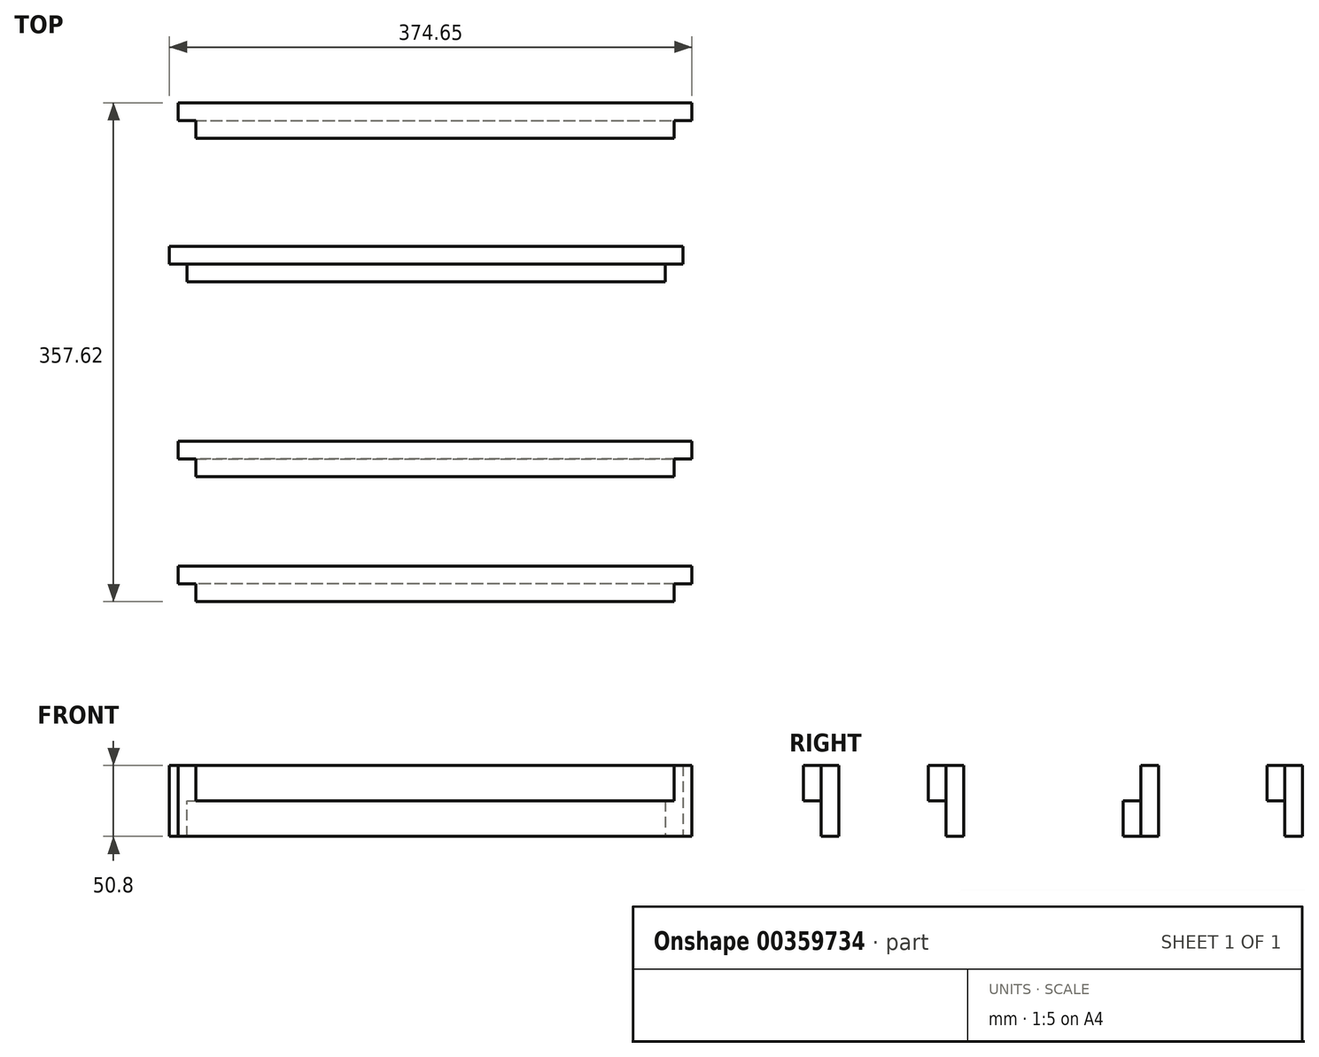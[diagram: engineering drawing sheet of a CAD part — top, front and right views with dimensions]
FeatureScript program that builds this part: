
annotation { "Feature Type Name" : "Feature", "Feature Type Description" : "" }
export const myFeature = defineFeature(function(context is Context, id is Id, definition is map)
    precondition{}
    {
        {
            var Q0;
            Q0=qCreatedBy(makeId("Top.planeOp"),FACE);
            var sketch = newSketch(context, id + "F0", { "sketchPlane" : qUnion([Q0])});
            skLineSegment(sketch, "E0.bottom", {"start": v(-184.15, 57.47) * mm, "end": v(184.15, 57.47) * mm});
            skLineSegment(sketch, "E0.top", {"start": v(-184.15, 32.07) * mm, "end": v(184.15, 32.07) * mm});
            skLineSegment(sketch, "E0.left", {"start": v(-184.15, 57.47) * mm, "end": v(-184.15, 32.07) * mm});
            skLineSegment(sketch, "E0.right", {"start": v(184.15, 57.47) * mm, "end": v(184.15, 32.07) * mm});
            skLineSegment(sketch, "E1.MirrorCS", {"start": v(-184.15, -32.07) * mm, "end": v(184.15, -32.07) * mm});
            skLineSegment(sketch, "E2.MirrorCS", {"start": v(-184.15, -57.47) * mm, "end": v(-184.15, -32.07) * mm});
            skLineSegment(sketch, "E3.MirrorCS", {"start": v(-184.15, -57.47) * mm, "end": v(184.15, -57.47) * mm});
            skLineSegment(sketch, "E4.MirrorCS", {"start": v(184.15, -57.47) * mm, "end": v(184.15, -32.07) * mm});
            skLineSegment(sketch, "E5.MirrorCS", {"start": v(-190.5, 274.75) * mm, "end": v(190.5, 274.75) * mm});
            skLineSegment(sketch, "E6.MirrorCS", {"start": v(-190.5, 300.15) * mm, "end": v(190.5, 300.15) * mm});
            skLineSegment(sketch, "E7.MirrorCS", {"start": v(-184.15, 274.75) * mm, "end": v(-184.15, 301.06) * mm});
            skLineSegment(sketch, "E8.MirrorCS", {"start": v(184.15, 274.75) * mm, "end": v(184.15, 301.06) * mm});
            skLineSegment(sketch, "E9.MirrorCS", {"start": v(-190.5, 171.65) * mm, "end": v(177.8, 171.65) * mm});
            skLineSegment(sketch, "E10.MirrorCS", {"start": v(-196.85, 197.05) * mm, "end": v(184.15, 197.05) * mm});
            skLineSegment(sketch, "E11.MirrorCS", {"start": v(-190.5, 170.74) * mm, "end": v(-190.5, 197.05) * mm});
            skLineSegment(sketch, "E12.MirrorCS", {"start": v(177.8, 170.74) * mm, "end": v(177.8, 197.05) * mm});
            skLineSegment(sketch, "E13", {"start": v(-6.35, 171.65) * mm, "end": v(-6.35, 197.05) * mm});
            skLineSegment(sketch, "E14", {"start": v(0, 274.75) * mm, "end": v(0, 300.15) * mm});
            skLineSegment(sketch, "E15", {"start": v(0, -57.47) * mm, "end": v(0, -32.07) * mm});
            skSolve(sketch);
        }
        {
            var Q0;
            Q0 = qSketchRegion(id + "F0", true);
            extrude(context, id + "F1", {"entities" : qUnion([Q0]), "depth" : 50.8 * mm});
        }
        {
            var Q0;
            Q0=makeQuery(id+"F1.opExtrude","CAP_FACE",FACE,{"disambiguationData":[OSD([sQuery(id+"F0.wireOp",EDGE,"E5.MirrorCS"),sQuery(id+"F0.wireOp",EDGE,"E6.MirrorCS"),sQuery(id+"F0.wireOp",EDGE,"E7.MirrorCS"),sQuery(id+"F0.wireOp",EDGE,"E8.MirrorCS")])],"isStart":false});
            var sketch = newSketch(context, id + "F2", { "sketchPlane" : qUnion([Q0])});
            skLineSegment(sketch, "E16", {"start": v(-184.15, 287.45) * mm, "end": v(-171.45, 287.45) * mm});
            skLineSegment(sketch, "E17", {"start": v(-171.45, 287.45) * mm, "end": v(-171.45, 274.75) * mm});
            skLineSegment(sketch, "E18", {"start": v(-171.45, 274.75) * mm, "end": v(-184.15, 274.75) * mm});
            skLineSegment(sketch, "E19", {"start": v(-184.15, 274.75) * mm, "end": v(-184.15, 287.45) * mm});
            skLineSegment(sketch, "E20", {"start": v(0, 274.75) * mm, "end": v(0, 300.15) * mm});
            skLineSegment(sketch, "E21.MirrorCS", {"start": v(184.15, 287.45) * mm, "end": v(171.45, 287.45) * mm});
            skLineSegment(sketch, "E22.MirrorCS", {"start": v(171.45, 287.45) * mm, "end": v(171.45, 274.75) * mm});
            skLineSegment(sketch, "E23.MirrorCS", {"start": v(171.45, 274.75) * mm, "end": v(184.15, 274.75) * mm});
            skLineSegment(sketch, "E24.MirrorCS", {"start": v(184.15, 274.75) * mm, "end": v(184.15, 287.45) * mm});
            skSolve(sketch);
        }
        {
            var Q0;
            Q0=makeQuery(id+"F2.imprint","IMPRINT",FACE,{"disambiguationData":[TD([[makeQuery(id+"F2.imprint","IMPRINT",EDGE,{"derivedFrom":sQuery(id+"F2.wireOp",EDGE,"E16")}),-1.0]])]});
            extrude(context, id + "F3", {"entities" : qUnion([Q0]), "operationType" : NewBodyOperationType.REMOVE, "oppositeDirection" : true, "depth" : 61.2 * mm});
        }
        {
            var Q0;
            Q0=makeQuery(id+"F1.opExtrude","CAP_FACE",FACE,{"disambiguationData":[OSD([sQuery(id+"F0.wireOp",EDGE,"E9.MirrorCS"),sQuery(id+"F0.wireOp",EDGE,"E10.MirrorCS"),sQuery(id+"F0.wireOp",EDGE,"E11.MirrorCS"),sQuery(id+"F0.wireOp",EDGE,"E12.MirrorCS")])],"isStart":false});
            var sketch = newSketch(context, id + "F4", { "sketchPlane" : qUnion([Q0])});
            skPoint(sketch, "E25.oppositeSnap0", {"position": v(-190.5, 184.35) * mm});
            skLineSegment(sketch, "E25.bottom", {"start": v(-190.5, 171.65) * mm, "end": v(-177.8, 171.65) * mm});
            skLineSegment(sketch, "E25.top", {"start": v(-190.5, 184.35) * mm, "end": v(-177.8, 184.35) * mm});
            skLineSegment(sketch, "E25.left", {"start": v(-190.5, 171.65) * mm, "end": v(-190.5, 184.35) * mm});
            skLineSegment(sketch, "E25.right", {"start": v(-177.8, 171.65) * mm, "end": v(-177.8, 184.35) * mm});
            skSolve(sketch);
        }
        {
            var Q0;
            Q0 = qSketchRegion(id + "F4", true);
            extrude(context, id + "F5", {"entities" : qUnion([Q0]), "operationType" : NewBodyOperationType.REMOVE, "oppositeDirection" : true, "depth" : 76.2 * mm});
        }
        {
            var Q0;
            Q0=makeQuery(id+"F1.opExtrude","SWEPT_FACE",FACE,{"disambiguationData":[OSD([sQuery(id+"F0.wireOp",EDGE,"E0.left")])]});
            var sketch = newSketch(context, id + "F6", { "sketchPlane" : qUnion([Q0])});
            skLineSegment(sketch, "E26.bottom", {"start": v(-44.77, 0) * mm, "end": v(-32.07, 0) * mm});
            skLineSegment(sketch, "E26.top", {"start": v(-44.77, 50.8) * mm, "end": v(-32.07, 50.8) * mm});
            skLineSegment(sketch, "E26.left", {"start": v(-44.77, 0) * mm, "end": v(-44.77, 50.8) * mm});
            skLineSegment(sketch, "E26.right", {"start": v(-32.07, 0) * mm, "end": v(-32.07, 50.8) * mm});
            skSolve(sketch);
        }
        {
            var Q0;
            Q0 = qSketchRegion(id + "F6", true);
            extrude(context, id + "F7", {"entities" : qUnion([Q0]), "operationType" : NewBodyOperationType.REMOVE, "oppositeDirection" : true, "depth" : 12.7 * mm});
        }
        {
            var Q0;
            Q0=makeQuery(id+"F1.opExtrude","SWEPT_FACE",FACE,{"disambiguationData":[OSD([sQuery(id+"F0.wireOp",EDGE,"E2.MirrorCS")])]});
            var sketch = newSketch(context, id + "F8", { "sketchPlane" : qUnion([Q0])});
            skLineSegment(sketch, "E27.bottom", {"start": v(44.77, 0) * mm, "end": v(57.47, 0) * mm});
            skLineSegment(sketch, "E27.top", {"start": v(44.77, 50.8) * mm, "end": v(57.47, 50.8) * mm});
            skLineSegment(sketch, "E27.left", {"start": v(44.77, 0) * mm, "end": v(44.77, 50.8) * mm});
            skLineSegment(sketch, "E27.right", {"start": v(57.47, 0) * mm, "end": v(57.47, 50.8) * mm});
            skSolve(sketch);
        }
        {
            var Q0;
            Q0 = qSketchRegion(id + "F8", true);
            extrude(context, id + "F9", {"entities" : qUnion([Q0]), "operationType" : NewBodyOperationType.REMOVE, "oppositeDirection" : true, "depth" : 12.7 * mm});
        }
        {
            var Q0;
            Q0 = qSketchRegion(id + "F2", true);
            extrude(context, id + "F10", {"entities" : qUnion([Q0]), "operationType" : NewBodyOperationType.REMOVE, "oppositeDirection" : true, "depth" : 50.8 * mm});
        }
        {
            var Q0;
            Q0=makeQuery(id+"F1.opExtrude","SWEPT_FACE",FACE,{"disambiguationData":[OSD([sQuery(id+"F0.wireOp",EDGE,"E12.MirrorCS")])]});
            var sketch = newSketch(context, id + "F11", { "sketchPlane" : qUnion([Q0])});
            skLineSegment(sketch, "E28.bottom", {"start": v(184.35, 50.8) * mm, "end": v(171.65, 50.8) * mm});
            skLineSegment(sketch, "E28.top", {"start": v(184.35, 0) * mm, "end": v(171.65, 0) * mm});
            skLineSegment(sketch, "E28.left", {"start": v(184.35, 50.8) * mm, "end": v(184.35, 0) * mm});
            skLineSegment(sketch, "E28.right", {"start": v(171.65, 50.8) * mm, "end": v(171.65, 0) * mm});
            skSolve(sketch);
        }
        {
            var Q0;
            Q0=makeQuery(id+"F11.imprint","IMPRINT",FACE,{"disambiguationData":[TD([[makeQuery(id+"F11.imprint","IMPRINT",EDGE,{"derivedFrom":sQuery(id+"F11.wireOp",EDGE,"E28.bottom")}),-1.0]])]});
            extrude(context, id + "F12", {"entities" : qUnion([Q0]), "operationType" : NewBodyOperationType.REMOVE, "oppositeDirection" : true, "depth" : 12.7 * mm});
        }
        {
            var Q0;
            Q0=makeQuery(id+"F1.opExtrude","SWEPT_FACE",FACE,{"disambiguationData":[OSD([sQuery(id+"F0.wireOp",EDGE,"E0.right")])]});
            var sketch = newSketch(context, id + "F13", { "sketchPlane" : qUnion([Q0])});
            skLineSegment(sketch, "E29.bottom", {"start": v(44.77, 50.8) * mm, "end": v(32.07, 50.8) * mm});
            skLineSegment(sketch, "E29.top", {"start": v(44.77, 0) * mm, "end": v(32.07, 0) * mm});
            skLineSegment(sketch, "E29.left", {"start": v(44.77, 50.8) * mm, "end": v(44.77, 0) * mm});
            skLineSegment(sketch, "E29.right", {"start": v(32.07, 50.8) * mm, "end": v(32.07, 0) * mm});
            skSolve(sketch);
        }
        {
            var Q0;
            Q0 = qSketchRegion(id + "F13", true);
            extrude(context, id + "F14", {"entities" : qUnion([Q0]), "operationType" : NewBodyOperationType.REMOVE, "oppositeDirection" : true, "depth" : 12.7 * mm});
        }
        {
            var Q0;
            Q0=makeQuery(id+"F1.opExtrude","CAP_FACE",FACE,{"disambiguationData":[OSD([sQuery(id+"F0.wireOp",EDGE,"E1.MirrorCS"),sQuery(id+"F0.wireOp",EDGE,"E2.MirrorCS"),sQuery(id+"F0.wireOp",EDGE,"E3.MirrorCS"),sQuery(id+"F0.wireOp",EDGE,"E4.MirrorCS")])],"isStart":true});
            var sketch = newSketch(context, id + "F15", { "sketchPlane" : qUnion([Q0])});
            skLineSegment(sketch, "E30", {"start": v(184.15, 44.77) * mm, "end": v(171.45, 44.77) * mm});
            skPoint(sketch, "E30.endSnap0", {"position": v(184.15, 44.77) * mm});
            skLineSegment(sketch, "E31", {"start": v(171.45, 44.77) * mm, "end": v(171.45, 32.07) * mm});
            skLineSegment(sketch, "E32", {"start": v(171.45, 32.07) * mm, "end": v(184.15, 32.07) * mm});
            skLineSegment(sketch, "E33", {"start": v(184.15, 32.07) * mm, "end": v(184.15, 44.77) * mm});
            skLineSegment(sketch, "E34", {"start": v(171.45, 44.77) * mm, "end": v(171.45, 57.47) * mm});
            skLineSegment(sketch, "E35", {"start": v(171.45, 57.47) * mm, "end": v(184.15, 57.47) * mm});
            skLineSegment(sketch, "E36", {"start": v(184.15, 57.47) * mm, "end": v(184.15, 44.77) * mm});
            skSolve(sketch);
        }
        {
            var Q0;
            Q0=makeQuery(id+"F15.imprint","IMPRINT",FACE,{"disambiguationData":[TD([[makeQuery(id+"F15.imprint","IMPRINT",EDGE,{"derivedFrom":sQuery(id+"F15.wireOp",EDGE,"E30")}),-1.0]])]});
            extrude(context, id + "F16", {"entities" : qUnion([Q0]), "operationType" : NewBodyOperationType.REMOVE, "oppositeDirection" : true, "depth" : 90.68 * mm});
        }
        {
            var Q0;
            Q0=makeQuery(id+"F9.boolean.opBoolean","COPY",FACE,{"derivedFrom":makeQuery(id+"F9.opExtrude","CAP_FACE",FACE,{"disambiguationData":[OSD([sQuery(id+"F8.wireOp",EDGE,"E27.bottom"),sQuery(id+"F8.wireOp",EDGE,"E27.top"),sQuery(id+"F8.wireOp",EDGE,"E27.left"),sQuery(id+"F8.wireOp",EDGE,"E27.right")])],"isStart":false})});
            var sketch = newSketch(context, id + "F17", { "sketchPlane" : qUnion([Q0])});
            skLineSegment(sketch, "E37", {"start": v(44.77, 50.8) * mm, "end": v(44.77, 0) * mm});
            skLineSegment(sketch, "E38", {"start": v(44.77, 0) * mm, "end": v(44.77, 25.4) * mm});
            skLineSegment(sketch, "E39", {"start": v(44.77, 25.4) * mm, "end": v(57.47, 25.4) * mm});
            skLineSegment(sketch, "E40", {"start": v(57.47, 25.4) * mm, "end": v(57.47, 0) * mm});
            skLineSegment(sketch, "E41", {"start": v(57.47, 0) * mm, "end": v(44.77, 0) * mm});
            skSolve(sketch);
        }
        {
            var Q0;
            Q0 = qSketchRegion(id + "F17", true);
            extrude(context, id + "F18", {"entities" : qUnion([Q0]), "operationType" : NewBodyOperationType.REMOVE, "oppositeDirection" : true, "depth" : 431.8 * mm});
        }
        {
            var Q0;
            Q0=makeQuery(id+"F14.boolean.opBoolean","COPY",FACE,{"derivedFrom":makeQuery(id+"F14.opExtrude","CAP_FACE",FACE,{"disambiguationData":[OSD([sQuery(id+"F13.wireOp",EDGE,"E29.bottom"),sQuery(id+"F13.wireOp",EDGE,"E29.top"),sQuery(id+"F13.wireOp",EDGE,"E29.left"),sQuery(id+"F13.wireOp",EDGE,"E29.right")])],"isStart":false})});
            var sketch = newSketch(context, id + "F19", { "sketchPlane" : qUnion([Q0])});
            skLineSegment(sketch, "E42.bottom", {"start": v(32.07, 0) * mm, "end": v(44.77, 0) * mm});
            skLineSegment(sketch, "E42.top", {"start": v(32.07, 25.4) * mm, "end": v(44.77, 25.4) * mm});
            skLineSegment(sketch, "E42.left", {"start": v(32.07, 0) * mm, "end": v(32.07, 25.4) * mm});
            skLineSegment(sketch, "E42.right", {"start": v(44.77, 0) * mm, "end": v(44.77, 25.4) * mm});
            skSolve(sketch);
        }
        {
            var Q0;
            Q0 = qSketchRegion(id + "F19", true);
            extrude(context, id + "F20", {"entities" : qUnion([Q0]), "operationType" : NewBodyOperationType.REMOVE, "oppositeDirection" : true, "depth" : 457.2 * mm});
        }
        {
            var Q0;
            Q0=makeQuery(id+"F12.boolean.opBoolean","COPY",FACE,{"derivedFrom":makeQuery(id+"F12.opExtrude","CAP_FACE",FACE,{"disambiguationData":[OSD([sQuery(id+"F11.wireOp",EDGE,"E28.bottom"),sQuery(id+"F11.wireOp",EDGE,"E28.top"),sQuery(id+"F11.wireOp",EDGE,"E28.left"),sQuery(id+"F11.wireOp",EDGE,"E28.right")])],"isStart":false})});
            var sketch = newSketch(context, id + "F21", { "sketchPlane" : qUnion([Q0])});
            skLineSegment(sketch, "E43.bottom", {"start": v(171.65, 0) * mm, "end": v(184.35, 0) * mm});
            skLineSegment(sketch, "E43.top", {"start": v(171.65, 25.4) * mm, "end": v(184.35, 25.4) * mm});
            skLineSegment(sketch, "E43.left", {"start": v(171.65, 0) * mm, "end": v(171.65, 25.4) * mm});
            skLineSegment(sketch, "E43.right", {"start": v(184.35, 0) * mm, "end": v(184.35, 25.4) * mm});
            skSolve(sketch);
        }
        {
            var Q0;
            Q0 = qSketchRegion(id + "F21", true);
            extrude(context, id + "F22", {"entities" : qUnion([Q0]), "operationType" : NewBodyOperationType.REMOVE, "oppositeDirection" : true, "depth" : 457.2 * mm});
        }
        {
            var Q0;
            Q0=makeQuery(id+"F10.boolean.opBoolean","COPY",FACE,{"derivedFrom":makeQuery(id+"F10.opExtrude","SWEPT_FACE",FACE,{"disambiguationData":[OSD([sQuery(id+"F2.wireOp",EDGE,"E22.MirrorCS")])]})});
            var sketch = newSketch(context, id + "F23", { "sketchPlane" : qUnion([Q0])});
            skLineSegment(sketch, "E44.bottom", {"start": v(274.75, 0) * mm, "end": v(287.45, 0) * mm});
            skLineSegment(sketch, "E44.top", {"start": v(274.75, 25.4) * mm, "end": v(287.45, 25.4) * mm});
            skLineSegment(sketch, "E44.left", {"start": v(274.75, 0) * mm, "end": v(274.75, 25.4) * mm});
            skLineSegment(sketch, "E44.right", {"start": v(287.45, 0) * mm, "end": v(287.45, 25.4) * mm});
            skSolve(sketch);
        }
        {
            var Q0;
            Q0 = qSketchRegion(id + "F23", true);
            extrude(context, id + "F24", {"entities" : qUnion([Q0]), "operationType" : NewBodyOperationType.REMOVE, "oppositeDirection" : true, "depth" : 431.8 * mm});
        }
        {
            var Q0;
            Q0=makeQuery(id+"F12.boolean.opBoolean","COPY",FACE,{"derivedFrom":makeQuery(id+"F12.opExtrude","CAP_FACE",FACE,{"disambiguationData":[OSD([sQuery(id+"F11.wireOp",EDGE,"E28.bottom"),sQuery(id+"F11.wireOp",EDGE,"E28.top"),sQuery(id+"F11.wireOp",EDGE,"E28.left"),sQuery(id+"F11.wireOp",EDGE,"E28.right")])],"isStart":false})});
            var sketch = newSketch(context, id + "F25", { "sketchPlane" : qUnion([Q0])});
            skLineSegment(sketch, "E45", {"start": v(171.65, 25.4) * mm, "end": v(184.35, 25.4) * mm});
            skSolve(sketch);
        }
        {
            var Q0;
            Q0=makeQuery(id+"F22.boolean.opBoolean","COPY",FACE,{"derivedFrom":makeQuery(id+"F22.opExtrude","SWEPT_FACE",FACE,{"disambiguationData":[OSD([sQuery(id+"F21.wireOp",EDGE,"E43.top")])]})});
            extrude(context, id + "F26", {"entities" : qUnion([Q0]), "operationType" : NewBodyOperationType.ADD, "depth" : 25.4 * mm});
        }
        {
            var Q0;
            Q0=makeQuery(id+"F25.imprint","IMPRINT",FACE,{"disambiguationData":[TD([[makeQuery(id+"F25.imprint","IMPRINT",EDGE,{"derivedFrom":sQuery(id+"F25.wireOp",EDGE,"E45")}),1.0]])]});
            extrude(context, id + "F27", {"entities" : qUnion([Q0]), "operationType" : NewBodyOperationType.REMOVE, "oppositeDirection" : true, "depth" : 685.8 * mm});
        }
    });
